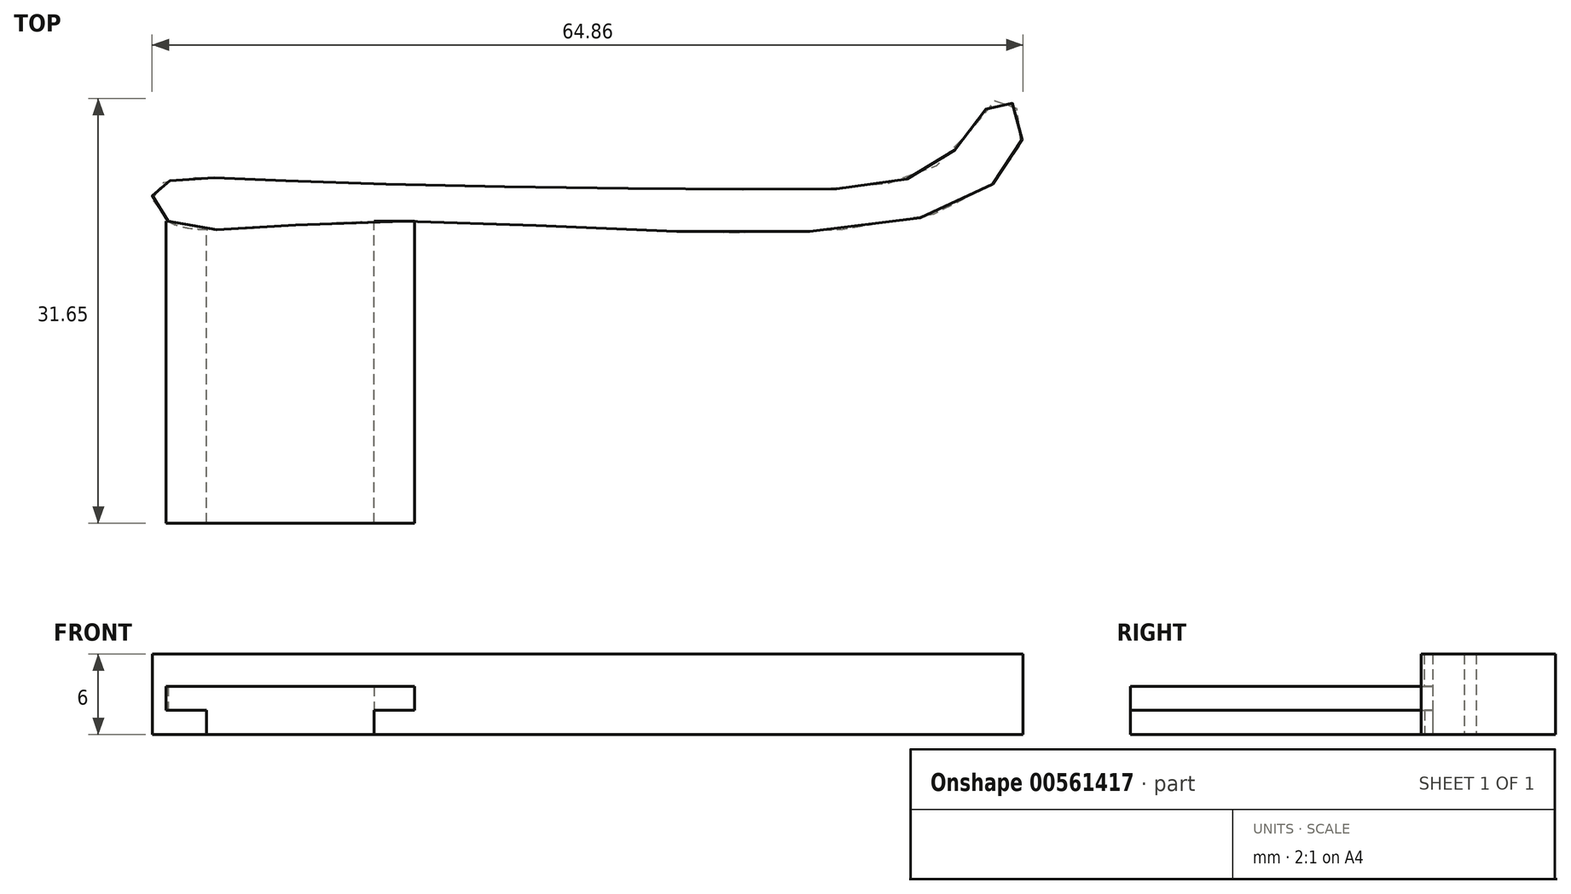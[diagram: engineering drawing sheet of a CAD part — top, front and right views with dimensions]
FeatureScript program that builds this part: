
annotation { "Feature Type Name" : "Feature", "Feature Type Description" : "" }
export const myFeature = defineFeature(function(context is Context, id is Id, definition is map)
    precondition{}
    {
        {
            var Q0;
            Q0=qCreatedBy(makeId("Top.planeOp"),FACE);
            var sketch = newSketch(context, id + "F0", { "sketchPlane" : qUnion([Q0])});
            skLineSegment(sketch, "E0.bottom", {"start": v(6.25, -11.25) * mm, "end": v(-6.25, -11.25) * mm});
            skLineSegment(sketch, "E0.top", {"start": v(6.25, 11.25) * mm, "end": v(-6.25, 11.25) * mm});
            skLineSegment(sketch, "E0.left", {"start": v(6.25, -11.25) * mm, "end": v(6.25, 11.25) * mm});
            skLineSegment(sketch, "E0.right", {"start": v(-6.25, -11.25) * mm, "end": v(-6.25, 11.25) * mm});
            skPoint(sketch, "E0.middle", {"position": v(0, 0) * mm});
            skSolve(sketch);
        }
        {
            var Q0;
            Q0 = qSketchRegion(id + "F0", true);
            extrude(context, id + "F1", {"entities" : qUnion([Q0]), "depth" : 1.8 * mm, "offsetDistance" : 25 * mm});
        }
        {
            var Q0;
            Q0=makeQuery(id+"F1.opExtrude","CAP_FACE",FACE,{"disambiguationData":[OSD([sQuery(id+"F0.wireOp",EDGE,"E0.bottom"),sQuery(id+"F0.wireOp",EDGE,"E0.top"),sQuery(id+"F0.wireOp",EDGE,"E0.left"),sQuery(id+"F0.wireOp",EDGE,"E0.right")])],"isStart":false});
            var sketch = newSketch(context, id + "F2", { "sketchPlane" : qUnion([Q0])});
            skLineSegment(sketch, "E1.bottom", {"start": v(9.25, -11.25) * mm, "end": v(-9.25, -11.25) * mm});
            skLineSegment(sketch, "E1.top", {"start": v(9.25, 11.25) * mm, "end": v(-9.25, 11.25) * mm});
            skLineSegment(sketch, "E1.left", {"start": v(9.25, -11.25) * mm, "end": v(9.25, 11.25) * mm});
            skLineSegment(sketch, "E1.right", {"start": v(-9.25, -11.25) * mm, "end": v(-9.25, 11.25) * mm});
            skPoint(sketch, "E1.middle", {"position": v(0, 0) * mm});
            skSolve(sketch);
        }
        {
            var Q0;
            Q0 = qSketchRegion(id + "F2", true);
            extrude(context, id + "F3", {"entities" : qUnion([Q0]), "operationType" : NewBodyOperationType.ADD, "depth" : 1.8 * mm, "offsetDistance" : 25 * mm});
        }
        {
            var Q0;
            Q0=makeQuery(id+"F1.opExtrude","CAP_FACE",FACE,{"disambiguationData":[OSD([sQuery(id+"F0.wireOp",EDGE,"E0.bottom"),sQuery(id+"F0.wireOp",EDGE,"E0.top"),sQuery(id+"F0.wireOp",EDGE,"E0.left"),sQuery(id+"F0.wireOp",EDGE,"E0.right")])],"isStart":true});
            var sketch = newSketch(context, id + "F4", { "sketchPlane" : qUnion([Q0])});
            skLineSegment(sketch, "E2", {"start": v(-6.25, -11.25) * mm, "end": v(-9.1, -11.25) * mm});
            skFitSpline(sketch, "E3", {"points": [v(-9.1, -11.25) * mm, v(6.25, -11.25) * mm, v(49.1, -12.18) * mm, v(54.54, -18.5) * mm, v(52.84, -20.38) * mm, v(48.98, -16.04) * mm, v(35.51, -13.62) * mm, v(0, -14.25) * mm, v(-9.1, -14.25) * mm, v(-10.27, -13.29) * mm, v(-9.1, -11.25) * mm]});
            skSolve(sketch);
        }
        {
            var Q0;
            Q0 = qSketchRegion(id + "F4", true);
            extrude(context, id + "F5", {"entities" : qUnion([Q0]), "operationType" : NewBodyOperationType.ADD, "oppositeDirection" : true, "depth" : 6 * mm, "offsetDistance" : 25 * mm});
        }
    });
